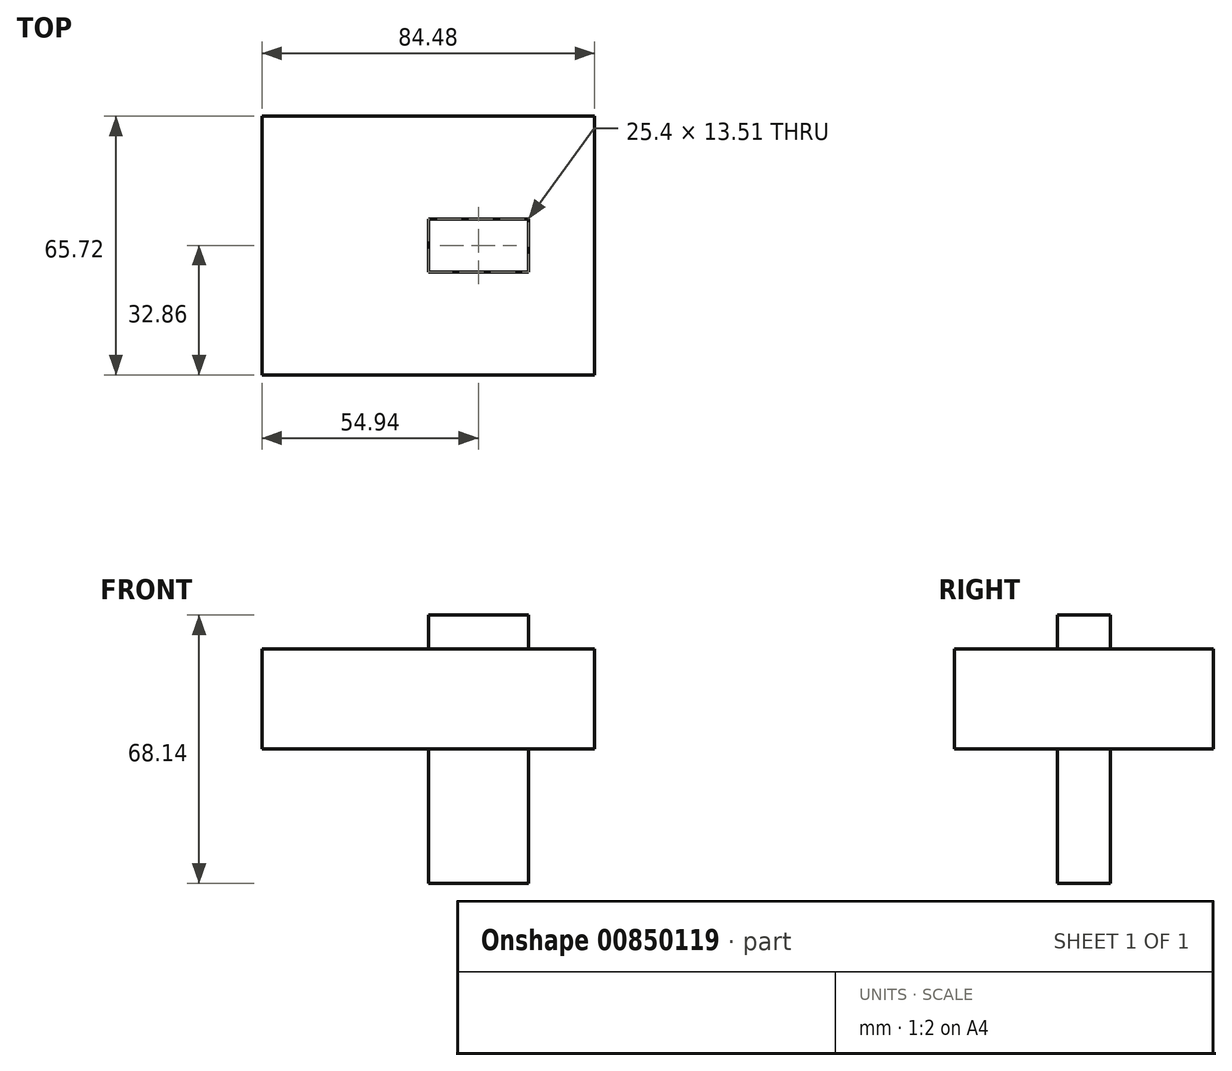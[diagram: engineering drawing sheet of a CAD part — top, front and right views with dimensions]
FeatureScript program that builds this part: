
annotation { "Feature Type Name" : "Feature", "Feature Type Description" : "" }
export const myFeature = defineFeature(function(context is Context, id is Id, definition is map)
    precondition{}
    {
        {
            var Q0;
            Q0=qCreatedBy(makeId("Right.planeOp"),FACE);
            var sketch = newSketch(context, id + "F0", { "sketchPlane" : qUnion([Q0])});
            skLineSegment(sketch, "E0.bottom", {"start": v(-6.75, 34.07) * mm, "end": v(6.75, 34.07) * mm});
            skLineSegment(sketch, "E0.top", {"start": v(-6.75, -34.07) * mm, "end": v(6.75, -34.07) * mm});
            skLineSegment(sketch, "E0.left", {"start": v(-6.75, 34.07) * mm, "end": v(-6.75, -34.07) * mm});
            skLineSegment(sketch, "E0.right", {"start": v(6.75, 34.07) * mm, "end": v(6.75, -34.07) * mm});
            skPoint(sketch, "E0.middle", {"position": v(0, 0) * mm});
            skSolve(sketch);
        }
        {
            var Q0;
            Q0=qCreatedBy(makeId("Top.planeOp"),FACE);
            var sketch = newSketch(context, id + "F1", { "sketchPlane" : qUnion([Q0])});
            skLineSegment(sketch, "E1.bottom", {"start": v(42.24, 32.86) * mm, "end": v(-42.24, 32.86) * mm});
            skLineSegment(sketch, "E1.top", {"start": v(42.24, -32.86) * mm, "end": v(-42.24, -32.86) * mm});
            skLineSegment(sketch, "E1.left", {"start": v(42.24, 32.86) * mm, "end": v(42.24, -32.86) * mm});
            skLineSegment(sketch, "E1.right", {"start": v(-42.24, 32.86) * mm, "end": v(-42.24, -32.86) * mm});
            skPoint(sketch, "E1.middle", {"position": v(0, 0) * mm});
            skSolve(sketch);
        }
        {
            var Q0;
            Q0=makeQuery(id+"F1.imprint","IMPRINT",FACE,{"disambiguationData":[TD([[makeQuery(id+"F1.imprint","IMPRINT",EDGE,{"derivedFrom":sQuery(id+"F1.wireOp",EDGE,"E1.bottom")}),1.0]])]});
            extrude(context, id + "F2", {"entities" : qUnion([Q0]), "depth" : 25.4 * mm, "offsetDistance" : 25.4 * mm});
        }
        {
            var Q0;
            Q0=makeQuery(id+"F0.imprint","IMPRINT",FACE,{"disambiguationData":[TD([[makeQuery(id+"F0.imprint","IMPRINT",EDGE,{"derivedFrom":sQuery(id+"F0.wireOp",EDGE,"E0.bottom")}),-1.0]])]});
            extrude(context, id + "F3", {"entities" : qUnion([Q0]), "operationType" : NewBodyOperationType.ADD, "depth" : 25.4 * mm, "offsetDistance" : 25.4 * mm});
        }
    });
